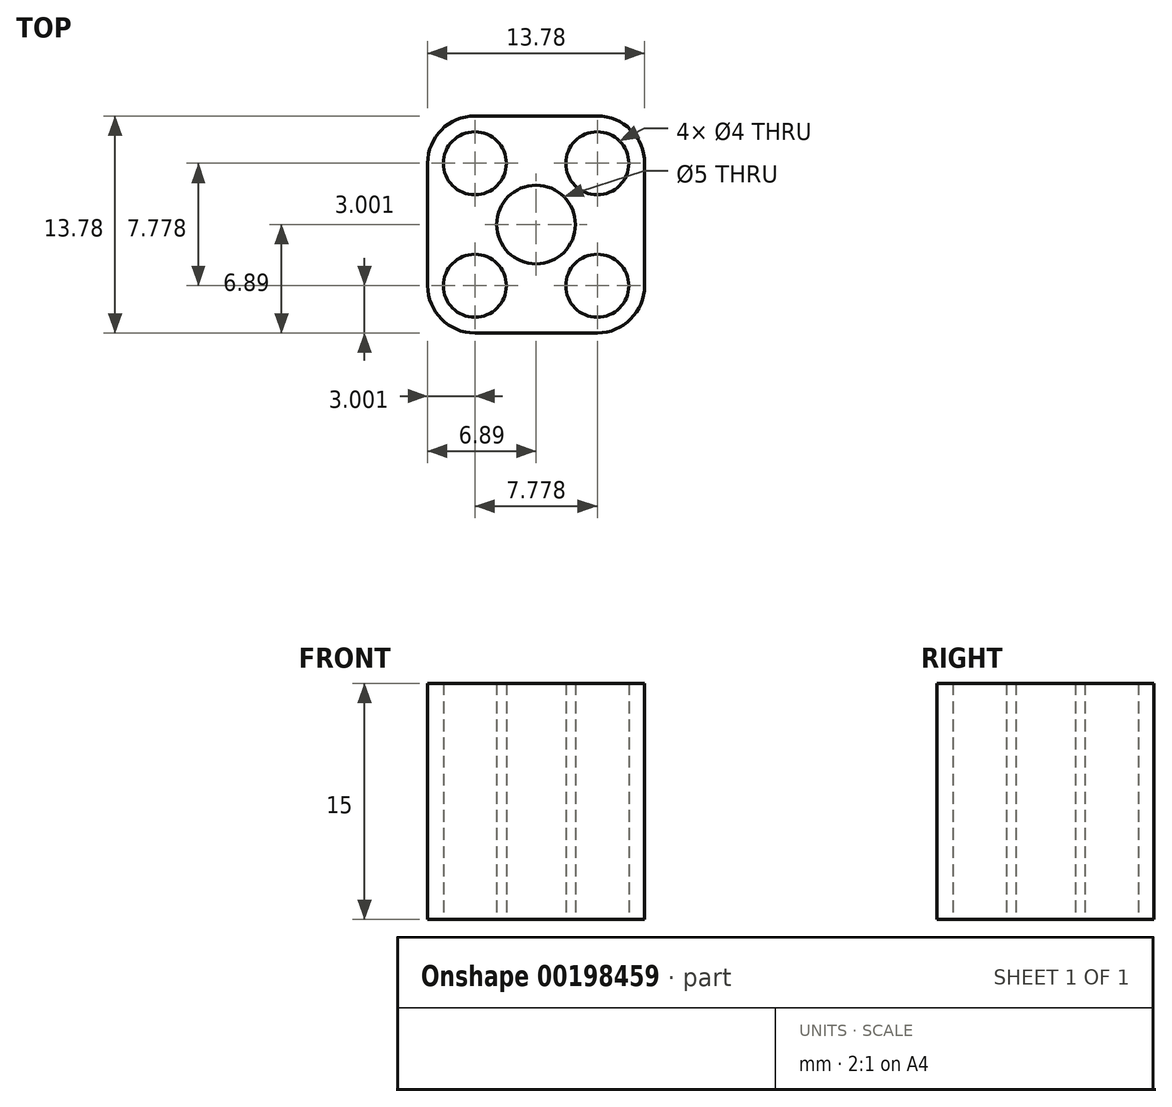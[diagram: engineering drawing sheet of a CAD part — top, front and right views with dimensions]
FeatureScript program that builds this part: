
annotation { "Feature Type Name" : "Feature", "Feature Type Description" : "" }
export const myFeature = defineFeature(function(context is Context, id is Id, definition is map)
    precondition{}
    {
        {
            var Q0;
            Q0=qCreatedBy(makeId("Top.planeOp"),FACE);
            var sketch = newSketch(context, id + "F0", { "sketchPlane" : qUnion([Q0])});
            skCircle(sketch, "E0", {"center": v(-3.89, -3.89) * mm, "radius": 2 * mm});
            skCircle(sketch, "E1.0.1.0", {"center": v(-3.89, 3.89) * mm, "radius": 2 * mm});
            skCircle(sketch, "E1.1.0.0", {"center": v(3.89, -3.89) * mm, "radius": 2 * mm});
            skCircle(sketch, "E1.1.1.0", {"center": v(3.89, 3.89) * mm, "radius": 2 * mm});
            skLineSegment(sketch, "E2.bottom", {"start": v(-3.89, -6.89) * mm, "end": v(3.89, -6.89) * mm});
            skLineSegment(sketch, "E2.top", {"start": v(-3.89, 6.89) * mm, "end": v(3.89, 6.89) * mm});
            skLineSegment(sketch, "E2.left", {"start": v(-6.89, -3.89) * mm, "end": v(-6.89, 3.89) * mm});
            skLineSegment(sketch, "E2.right", {"start": v(6.89, -3.89) * mm, "end": v(6.89, 3.89) * mm});
            skPoint(sketch, "E2.middle", {"position": v(0, 0) * mm});
            skPoint(sketch, "E3.visualSharp", {"position": v(-6.89, 6.89) * mm});
            skArc(sketch, "E3.filletArc", {"start": v(-3.89, 6.89) * mm, "mid": v(-6.01, 6.01) * mm, "end": v(-6.89, 3.89) * mm});
            skPoint(sketch, "E4.visualSharp", {"position": v(6.89, 6.89) * mm});
            skArc(sketch, "E4.filletArc", {"start": v(6.89, 3.89) * mm, "mid": v(6.01, 6.01) * mm, "end": v(3.89, 6.89) * mm});
            skPoint(sketch, "E5.visualSharp", {"position": v(6.89, -6.89) * mm});
            skArc(sketch, "E5.filletArc", {"start": v(3.89, -6.89) * mm, "mid": v(6.01, -6.01) * mm, "end": v(6.89, -3.89) * mm});
            skPoint(sketch, "E6.visualSharp", {"position": v(-6.89, -6.89) * mm});
            skArc(sketch, "E6.filletArc", {"start": v(-6.89, -3.89) * mm, "mid": v(-6.01, -6.01) * mm, "end": v(-3.89, -6.89) * mm});
            skCircle(sketch, "E7", {"center": v(0, 0) * mm, "radius": 2.5 * mm});
            skLineSegment(sketch, "E8", {"start": v(-3.89, -3.89) * mm, "end": v(3.89, -3.89) * mm, "construction": true});
            skLineSegment(sketch, "E9", {"start": v(-3.89, -3.89) * mm, "end": v(-3.89, 3.89) * mm, "construction": true});
            skLineSegment(sketch, "E10", {"start": v(-3.89, 3.89) * mm, "end": v(3.89, 3.89) * mm, "construction": true});
            skLineSegment(sketch, "E11", {"start": v(3.89, -3.89) * mm, "end": v(3.89, 3.89) * mm, "construction": true});
            skLineSegment(sketch, "E12", {"start": v(-3.89, -3.89) * mm, "end": v(3.89, 3.89) * mm});
            skSolve(sketch);
        }
        {
            var Q0;
            Q0 = qSketchRegion(id + "F0", true);
            extrude(context, id + "F1", {"entities" : qUnion([Q0]), "depth" : 15 * mm});
        }
    });
